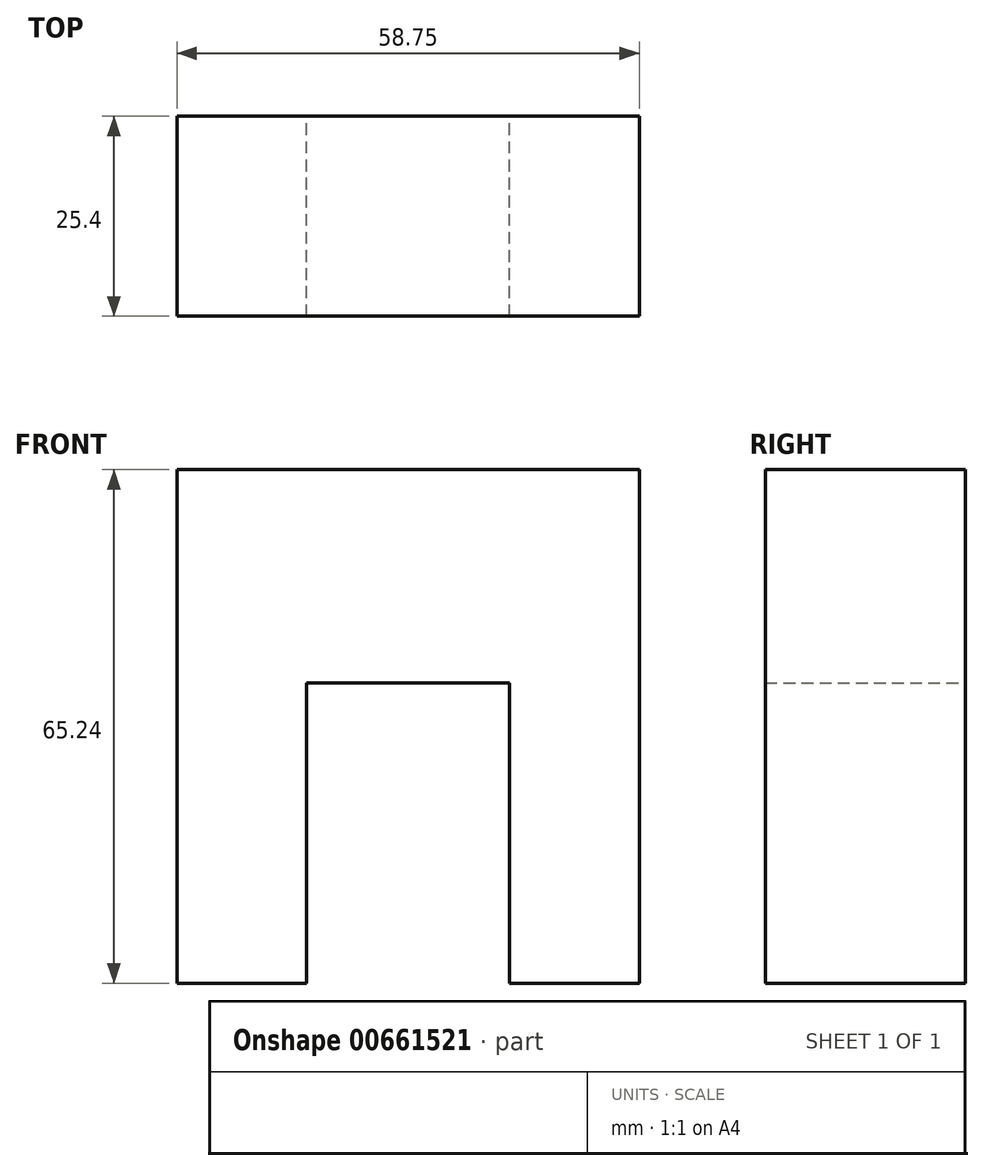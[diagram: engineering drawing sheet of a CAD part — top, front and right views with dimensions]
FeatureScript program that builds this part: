
annotation { "Feature Type Name" : "Feature", "Feature Type Description" : "" }
export const myFeature = defineFeature(function(context is Context, id is Id, definition is map)
    precondition{}
    {
        {
            var Q0;
            Q0=qCreatedBy(makeId("Front.planeOp"),FACE);
            var sketch = newSketch(context, id + "F0", { "sketchPlane" : qUnion([Q0])});
            skLineSegment(sketch, "E0", {"start": v(0, 0) * mm, "end": v(-42.25, 0) * mm});
            skLineSegment(sketch, "E1", {"start": v(-42.25, 0) * mm, "end": v(-42.25, -65.24) * mm});
            skLineSegment(sketch, "E2", {"start": v(-42.25, -65.24) * mm, "end": v(-25.75, -65.24) * mm});
            skLineSegment(sketch, "E3", {"start": v(-25.75, -65.24) * mm, "end": v(-25.75, -27.07) * mm});
            skLineSegment(sketch, "E4", {"start": v(-25.75, -27.07) * mm, "end": v(0, -27.07) * mm});
            skLineSegment(sketch, "E5", {"start": v(0, -27.07) * mm, "end": v(0, -65.24) * mm});
            skLineSegment(sketch, "E6", {"start": v(0, -65.24) * mm, "end": v(16.5, -65.24) * mm});
            skLineSegment(sketch, "E7", {"start": v(16.5, -65.24) * mm, "end": v(16.5, 0) * mm});
            skLineSegment(sketch, "E8", {"start": v(16.5, 0) * mm, "end": v(0, 0) * mm});
            skSolve(sketch);
        }
        {
            var Q0;
            Q0=makeQuery(id+"F0.imprint","IMPRINT",FACE,{"disambiguationData":[TD([[makeQuery(id+"F0.imprint","IMPRINT",EDGE,{"derivedFrom":sQuery(id+"F0.wireOp",EDGE,"E0")}),1.0]])]});
            extrude(context, id + "F1", {"entities" : qUnion([Q0]), "depth" : 25.4 * mm, "offsetDistance" : 25.4 * mm});
        }
    });
